# Revit family: Скамейка с вешалкой для раздевалок «Ювентус» Арт 20487
name_source: partatom
category: Антураж
revit_build: Autodesk Revit 2018 (Build: 20180423_1000(x64)
units: mm (PartAtom-declared; Revit-internal decimal feet)

## family parameters
Всегда вертикально = Да
Источник визуального образа = Геометрия семейства
На основе рабочей плоскости = Нет
Общий = Нет
При загрузке вырезать с полостями = Нет
Точка расчета площади = Нет

## types (3) — shared parameters
URL = https://hobbyka.ru
Артикул товара = Арт. 20487
Высота = 1785 мм
Группа модели = Скамейки для раздевалок
Изготовитель = ООО «Хоббика»
Изображение типоразмера = Скамейка с вешалкой для раздевалок «Ювентус» Арт 20487.jpg
Материал изделия = Сталь, дерево
Цвет каркаса = Сталь
Цвет крючков = Хром
Цвет лавки = Тик
Ширина = 425 мм

## per-type parameters (varying)
| type | Версия 1,2 м | Версия 1,5 м | Версия 2,0 м | Длина | Кол-во крючков | Л1 | Описание |
| Версия 1,2 м | Да | Нет | Нет | 1200 мм | 6 | 171 мм | Скамейка с вешалкой для раздевалок «Ювентус» 1,2 м |
| Версия 1,5 м | Нет | Да | Нет | 1500 мм | 8 | 167 мм | Скамейка с вешалкой для раздевалок «Ювентус» 1,5 м |
| Версия 2,0 м | Нет | Нет | Да | 2000 мм | 11 | 167 мм | Скамейка с вешалкой для раздевалок «Ювентус» 2,0 м |
